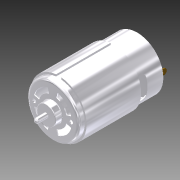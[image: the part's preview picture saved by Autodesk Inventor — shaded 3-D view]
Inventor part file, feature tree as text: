
AUTODESK INVENTOR PART (.ipt)
format: ipt  version: 2012 (Build 160160000, 160)  size: 343,552 bytes
history: native  units: mm (DEFAULTED — no unit token found)
features: sketch x15, extrude x13, fillet x3, plane x3, hole x2, mirror x2, pattern_circular x2, shell x1, chamfer x1
ambient origin geometry x8: Origin, YZ Plane, XZ Plane, XY Plane, X Axis, Y Axis, Z Axis, Center Point
bodies: Solid1 (feature_tree)
feature tree (42):
  extrude  "Extrusion1"  Depth=57.25mm TaperAngle=0.0deg
  fillet  "Fillet1"  Radius=2.0mm
  shell  "Shell1"  Thickness=0.62mm
  extrude  "Extrusion2"  Depth=4.5mm TaperAngle=0.0deg
  fillet  "Fillet2"  Radius=0.5mm
  extrude  "Extrusion3"  Depth=7.62mm TaperAngle=0.0deg
  fillet  "Fillet3"  Radius=1.6mm
  hole  "Hole1"  [1 undecoded]
  mirror  "Mirror1"
  extrude  "Extrusion4"  Depth=13.0mm
  pattern_circular  "Circular Pattern1"  Count=4 Angle=360.0deg
  plane  "Work Plane1"
  extrude  "Extrusion5"  Depth=0.62mm TaperAngle=0.0deg
  extrude  "Extrusion6"  Depth=0.62mm TaperAngle=0.0deg
  extrude  "Extrusion7"  Depth=3.0mm TaperAngle=0.0deg
  extrude  "Extrusion8"  Depth=0.8mm TaperAngle=0.0deg
  extrude  "Extrusion9"  Depth=1.0mm TaperAngle=0.0deg
  extrude  "Extrusion10"  Depth=3.15mm
  pattern_circular  "Circular Pattern2"  [2 undecoded]
  extrude  "Extrusion11"  Depth=1.0mm TaperAngle=0.0deg
  chamfer  "Chamfer1"  Distance=40.0mm Angle=360.0deg
  hole  "Hole2"  [1 undecoded]
  mirror  "Mirror2"
  plane  "Work Plane2"
  extrude  "Extrusion12"  Depth=3.8mm
  plane  "Work Plane3"
  extrude  "Extrusion13"  Depth=14.0mm
  sketch  "Sketch1"  dims[d0=35.5mm d1=57.25mm d2=0.0mm d3=2.0mm d4=0.62mm]
  sketch  "Sketch2"  dims[d5=13.0mm d6=4.5mm d7=0.0mm d8=0.5mm]
  sketch  "Sketch3"  dims[d9=3.2mm d10=7.62mm d11=0.0mm d12=1.6mm]
  sketch  "Sketch4"  dims[d13=12.5mm]
  sketch  "Sketch5"  dims[d14=2.5mm d15=6.0mm d16=4.0mm d17=2.0mm d18=14.3117mm d19=8.0mm d20=20.594885mm d21=15.0deg]
  sketch  "Sketch6"  dims[d22=15.0deg d23=13.0mm]
  sketch  "Sketch7"  dims[d24=9.5mm]
  sketch  "Sketch8"  dims[d25=10.0mm d26=0.0mm d27=40.0mm d29=360.0deg]
  sketch  "Sketch9"  dims[d30=-1.75mm d31=0.62mm d32=0.0mm]
  sketch  "Sketch10"  dims[d33=24.0mm d34=0.62mm d35=0.0mm]
  sketch  "Sketch11"  dims[d36=10.75mm d37=3.0mm d38=0.0mm]
  sketch  "Sketch12"  dims[d39=6.9mm d40=0.8mm d41=0.0mm]
  sketch  "Sketch13"  dims[d42=3.2mm d43=1.0mm d44=0.0mm]
  sketch  "Sketch14"  dims[d45=3.15mm d46=3.15mm]
  sketch  "Sketch15"  dims[d47=9.875mm d48=6.5mm d49=1.0mm d50=0.0mm d51=40.0mm d53=360.0deg d54=0.5mm d55=3.8mm d56=14.0mm d57=7.2mm d58=0.0mm d59=1.0mm d60=2.0mm d61=3.0mm d62=2.0mm d63=6.0mm d64=4.0mm d65=2.0mm d66=14.3117mm d67=1.0mm d68=20.594885mm d69=18.0mm d70=10.75mm d71=5.9mm d72=9.85mm d73=7.2mm d74=0.0mm d75=-4.0mm d76=38.0mm d77=3.5mm d78=37.0mm d79=0.0mm d80=45.0deg]
note: 4 required parameter values undecoded (feature->parameter linkage not recoverable at this tier; creation-order binding heuristic only, values carry confidence <= 0.55)
